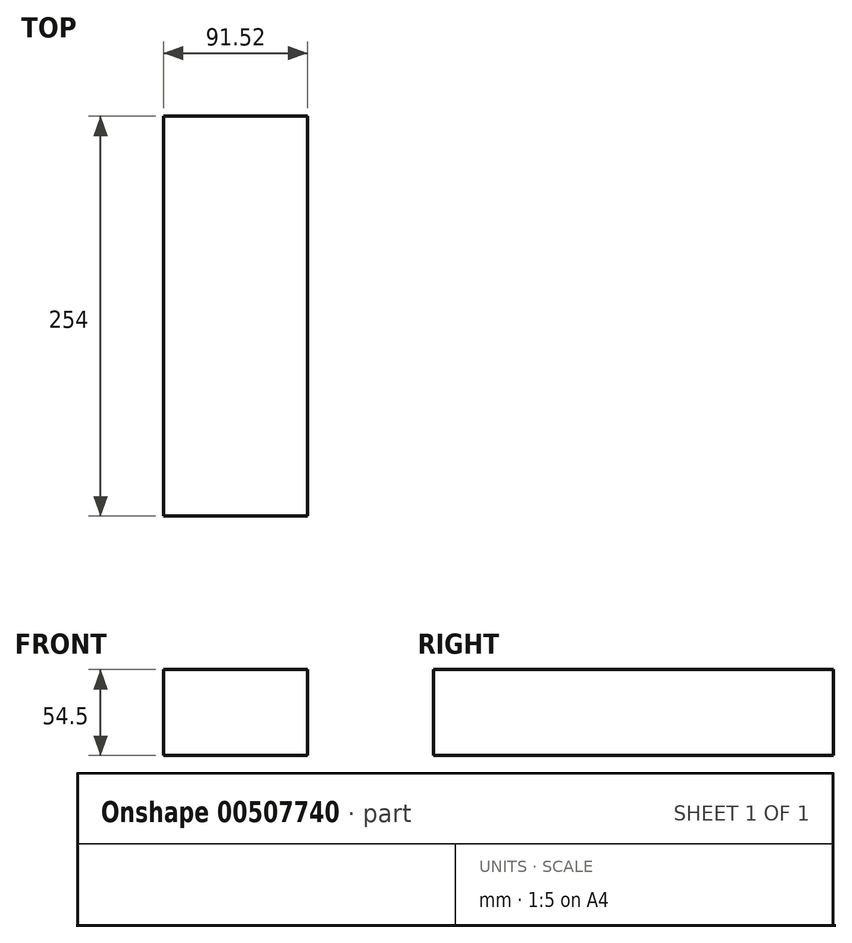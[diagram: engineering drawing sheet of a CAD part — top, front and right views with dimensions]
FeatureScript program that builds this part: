
annotation { "Feature Type Name" : "Feature", "Feature Type Description" : "" }
export const myFeature = defineFeature(function(context is Context, id is Id, definition is map)
    precondition{}
    {
        {
            var Q0;
            Q0=qCreatedBy(makeId("Front.planeOp"),FACE);
            var sketch = newSketch(context, id + "F0", { "sketchPlane" : qUnion([Q0])});
            skLineSegment(sketch, "E0.bottom", {"start": v(45.76, 27.25) * mm, "end": v(-45.76, 27.25) * mm});
            skLineSegment(sketch, "E0.top", {"start": v(45.76, -27.25) * mm, "end": v(-45.76, -27.25) * mm});
            skLineSegment(sketch, "E0.left", {"start": v(45.76, 27.25) * mm, "end": v(45.76, -27.25) * mm});
            skLineSegment(sketch, "E0.right", {"start": v(-45.76, 27.25) * mm, "end": v(-45.76, -27.25) * mm});
            skPoint(sketch, "E0.middle", {"position": v(0, 0) * mm});
            skSolve(sketch);
        }
        {
            var Q0;
            Q0=makeQuery(id+"F0.imprint","IMPRINT",FACE,{"disambiguationData":[TD([[makeQuery(id+"F0.imprint","IMPRINT",EDGE,{"derivedFrom":sQuery(id+"F0.wireOp",EDGE,"E0.bottom")}),1.0]])]});
            extrude(context, id + "F1", {"entities" : qUnion([Q0]), "depth" : 254 * mm});
        }
    });
